# Revit family: Fly Table SC5
name_source: partatom
category: Furniture
revit_build: Autodesk Revit 2017 (Build: 20171027_0315(x64)
units: mm (PartAtom-declared; Revit-internal decimal feet)

## family parameters
Always vertical = Yes
Cut with Voids When Loaded = No
OmniClass Number = 23.40.20.00
OmniClass Title = General Furniture and Specialties
Room Calculation Point = No
Shared = No
Work Plane-Based = No

## types (1)
- Fly Table SC5
    Base = &tradition Smoked Oak Oiled Vertical
    Depth = 60cm/23.6in
    Description = Pushing the idea of lounging to its fullest, Fly is a series that allows the user to sit, lie, rest, and relax. Unlike many of the sofas and easy chairs in Scandinavian design history, Fly does not impose any particular posture onto the sitter. The seat itself is optimised for comfort, with loose cushions for the back that can be arranged according to the user’s own needs.
    Design = Space Copenhagen
    Design Year = 2013
    Frame = &tradition Smoked Oak Oiled Horizontal
    Gliders = &tradition Felt Black
    Height = 26cm/10.2in
    Manufacturer = &tradition
    Model = Fly Table SC5
    Packaging Dimension Base = Wood H: 7cm/2.8in W:75cm/29.5in L: 126cm/49.6in
    Packaging Dimension Table Top = Marble H: 8cm/3.1in W: 67cm/26.4in L: 128cm/50.4in
    Table Top = &tradition Marble Honed Nero Marquina
    Type Comments = Fly Series
    URL = https://www.andtradition.com
    Variations Base = Available in white oiled oak. Available with 32 cm/12.6in high legs.
    Variations Table Top = Oiled Smoked Oak available with honed Pietra de Fossena marble. White Oiled Oak available with honed Bianco Carrara marble or honed Pietra de Fossena marble.
    Weight = 45kg
    Width = 120cm/47.2in

## geometry (parser evidence)
native form markers: Sweep x3
no freeform markers — native parametric forms only
